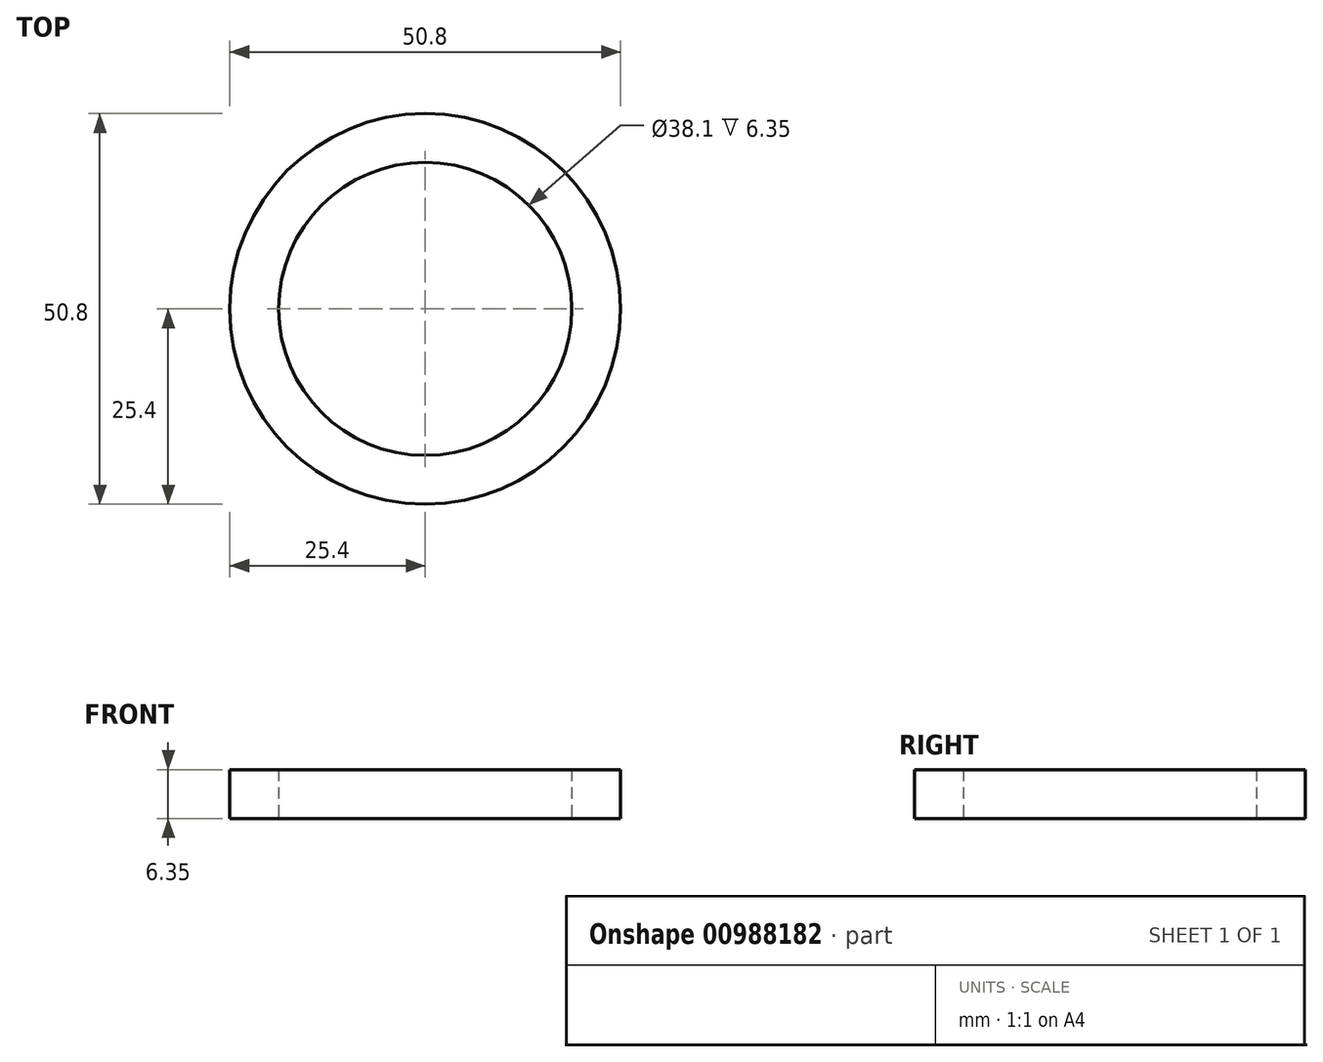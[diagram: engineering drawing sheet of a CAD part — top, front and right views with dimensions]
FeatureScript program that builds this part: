
annotation { "Feature Type Name" : "Feature", "Feature Type Description" : "" }
export const myFeature = defineFeature(function(context is Context, id is Id, definition is map)
    precondition{}
    {
        {
            var Q0;
            Q0=qCreatedBy(makeId("Top.planeOp"),FACE);
            var sketch = newSketch(context, id + "F0", { "sketchPlane" : qUnion([Q0])});
            skCircle(sketch, "E0", {"center": v(0, 0) * mm, "radius": 25.4 * mm});
            skCircle(sketch, "E1", {"center": v(0, 0) * mm, "radius": 19.05 * mm});
            skSolve(sketch);
        }
        {
            var Q0;
            Q0=makeQuery(id+"F0.imprint","IMPRINT",FACE,{"disambiguationData":[TD([[makeQuery(id+"F0.imprint","IMPRINT",EDGE,{"derivedFrom":sQuery(id+"F0.wireOp",EDGE,"E0")}),1.0]])]});
            extrude(context, id + "F1", {"entities" : qUnion([Q0]), "depth" : 6.35 * mm, "offsetDistance" : 25.4 * mm});
        }
    });
